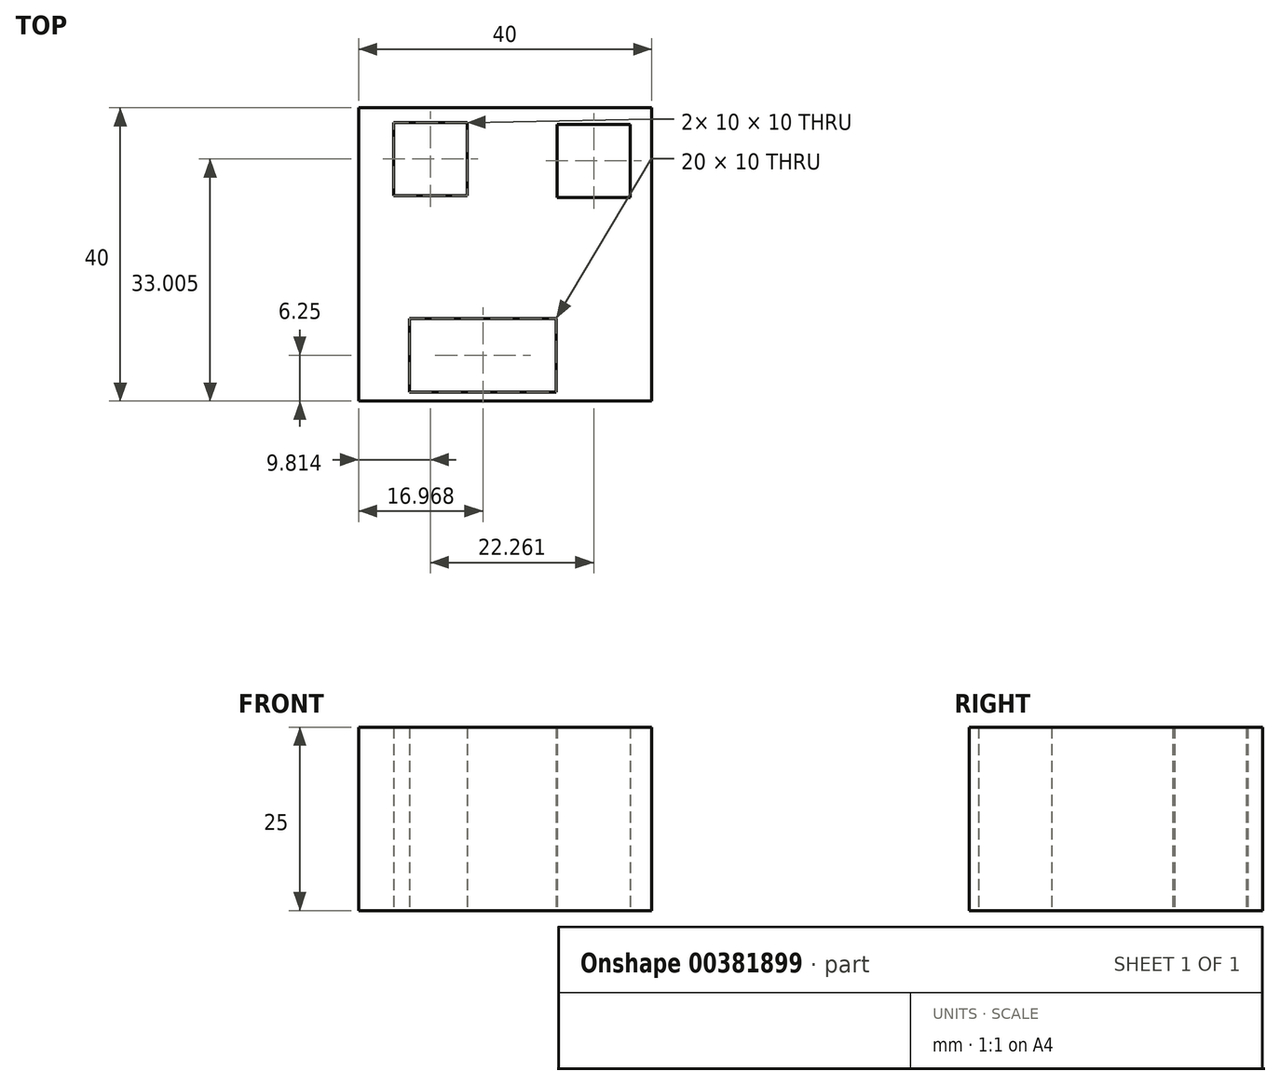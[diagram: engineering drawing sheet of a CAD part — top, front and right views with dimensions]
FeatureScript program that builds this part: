
annotation { "Feature Type Name" : "Feature", "Feature Type Description" : "" }
export const myFeature = defineFeature(function(context is Context, id is Id, definition is map)
    precondition{}
    {
        {
            var Q0;
            Q0=qCreatedBy(makeId("Top.planeOp"),FACE);
            var sketch = newSketch(context, id + "F0", { "sketchPlane" : qUnion([Q0])});
            skLineSegment(sketch, "E0", {"start": v(0, 0) * mm, "end": v(-40, 0) * mm});
            skLineSegment(sketch, "E1", {"start": v(-40, 0) * mm, "end": v(-40, 40) * mm});
            skLineSegment(sketch, "E2", {"start": v(-40, 40) * mm, "end": v(0, 40) * mm});
            skLineSegment(sketch, "E3", {"start": v(0, 40) * mm, "end": v(0, 0) * mm});
            skLineSegment(sketch, "E4", {"start": v(-35.19, 38) * mm, "end": v(-35.19, 28) * mm});
            skLineSegment(sketch, "E5", {"start": v(-35.19, 38) * mm, "end": v(-25.19, 38) * mm});
            skLineSegment(sketch, "E6", {"start": v(-25.19, 38) * mm, "end": v(-25.19, 28) * mm});
            skLineSegment(sketch, "E7", {"start": v(-25.19, 28) * mm, "end": v(-35.19, 28) * mm});
            skLineSegment(sketch, "E8", {"start": v(-12.93, 37.77) * mm, "end": v(-2.93, 37.77) * mm});
            skLineSegment(sketch, "E9", {"start": v(-12.93, 37.77) * mm, "end": v(-12.93, 27.77) * mm});
            skLineSegment(sketch, "E10", {"start": v(-12.93, 27.77) * mm, "end": v(-2.93, 27.77) * mm});
            skLineSegment(sketch, "E11", {"start": v(-2.93, 37.77) * mm, "end": v(-2.93, 27.77) * mm});
            skLineSegment(sketch, "E12", {"start": v(-33.03, 11.25) * mm, "end": v(-13.03, 11.25) * mm});
            skLineSegment(sketch, "E13", {"start": v(-13.03, 11.25) * mm, "end": v(-13.03, 1.25) * mm});
            skLineSegment(sketch, "E14", {"start": v(-33.03, 11.25) * mm, "end": v(-33.03, 1.25) * mm});
            skLineSegment(sketch, "E15", {"start": v(-33.03, 1.25) * mm, "end": v(-13.03, 1.25) * mm});
            skSolve(sketch);
        }
        {
            var Q0;
            Q0 = qSketchRegion(id + "F0", true);
            extrude(context, id + "F1", {"entities" : qUnion([Q0]), "depth" : 25 * mm});
        }
    });
